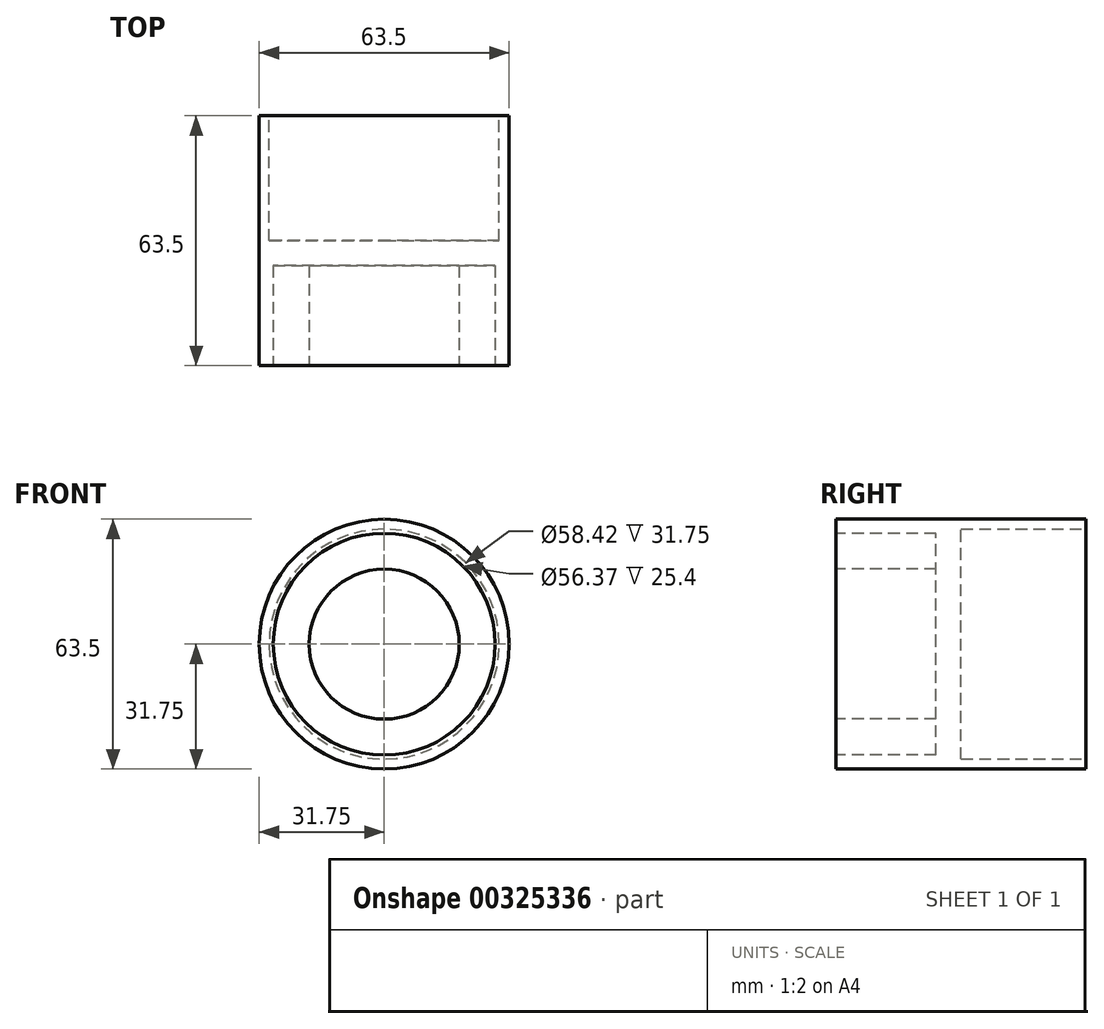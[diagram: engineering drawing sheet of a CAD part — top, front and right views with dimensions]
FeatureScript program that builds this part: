
annotation { "Feature Type Name" : "Feature", "Feature Type Description" : "" }
export const myFeature = defineFeature(function(context is Context, id is Id, definition is map)
    precondition{}
    {
        {
            var Q0;
            Q0=qCreatedBy(makeId("Front.planeOp"),FACE);
            var sketch = newSketch(context, id + "F0", { "sketchPlane" : qUnion([Q0])});
            skCircle(sketch, "E0", {"center": v(0, 0) * mm, "radius": 31.75 * mm});
            skSolve(sketch);
        }
        {
            var Q0;
            Q0 = qSketchRegion(id + "F0", true);
            extrude(context, id + "F1", {"entities" : qUnion([Q0]), "depth" : 63.5 * mm});
        }
        {
            var Q0;
            Q0=qCreatedBy(makeId("Front.planeOp"),FACE);
            var sketch = newSketch(context, id + "F2", { "sketchPlane" : qUnion([Q0])});
            skCircle(sketch, "E1.0", {"center": v(0, 0) * mm, "radius": 29.21 * mm});
            skSolve(sketch);
        }
        {
            var Q0;
            Q0 = qSketchRegion(id + "F2", true);
            extrude(context, id + "F3", {"entities" : qUnion([Q0]), "operationType" : NewBodyOperationType.REMOVE, "depth" : 31.75 * mm});
        }
        {
            var Q0;
            Q0=makeQuery(id+"F1.opExtrude","CAP_FACE",FACE,{"disambiguationData":[OSD([sQuery(id+"F0.wireOp",EDGE,"E0")])],"isStart":false});
            var sketch = newSketch(context, id + "F4", { "sketchPlane" : qUnion([Q0])});
            skCircle(sketch, "E2.0", {"center": v(0, 0) * mm, "radius": 19.05 * mm});
            skCircle(sketch, "E3.0", {"center": v(0, 0) * mm, "radius": 28.18 * mm});
            skSolve(sketch);
        }
        {
            var Q0;
            Q0 = qSketchRegion(id + "F4", true);
            extrude(context, id + "F5", {"entities" : qUnion([Q0]), "operationType" : NewBodyOperationType.REMOVE, "oppositeDirection" : true, "depth" : 25.4 * mm});
        }
    });
